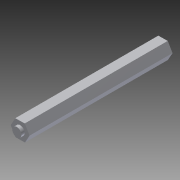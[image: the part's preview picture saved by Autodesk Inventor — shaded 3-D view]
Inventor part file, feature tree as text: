
AUTODESK INVENTOR PART (.ipt)
format: ipt  version: 2014 SP1 (Build 180222100, 222)  size: 94,720 bytes
history: native  units: in
note: dims shown in document units (in); Inventor stores cm internally (conversion verified against a paired STEP export)
features: extrude x4, sketch x4
ambient origin geometry x8: Origin, YZ Plane, XZ Plane, XY Plane, X Axis, Y Axis, Z Axis, Center Point
bodies: Solid1 (feature_tree)
feature tree (8):
  extrude  "Extrusion1"  Depth=0.5in TaperAngle=0.0deg
  extrude  "Extrusion2"  Depth=0.375in TaperAngle=0.0deg
  extrude  "Extrusion3"  [1 undecoded]
  extrude  "Extrusion4"  [1 undecoded]
  sketch  "Sketch1"  dims[d0=0.5in d1=4.0in d2=0.0in]
  sketch  "Sketch2"  dims[d3=0.01in d4=0.0in d5=0.375in d6=0.0in]
  sketch  "Sketch3"  dims[d7=0.1in d8=0.0in]
  sketch  "Sketch4"
note: 2 required parameter values undecoded (feature->parameter linkage not recoverable at this tier; creation-order binding heuristic only, values carry confidence <= 0.55)
